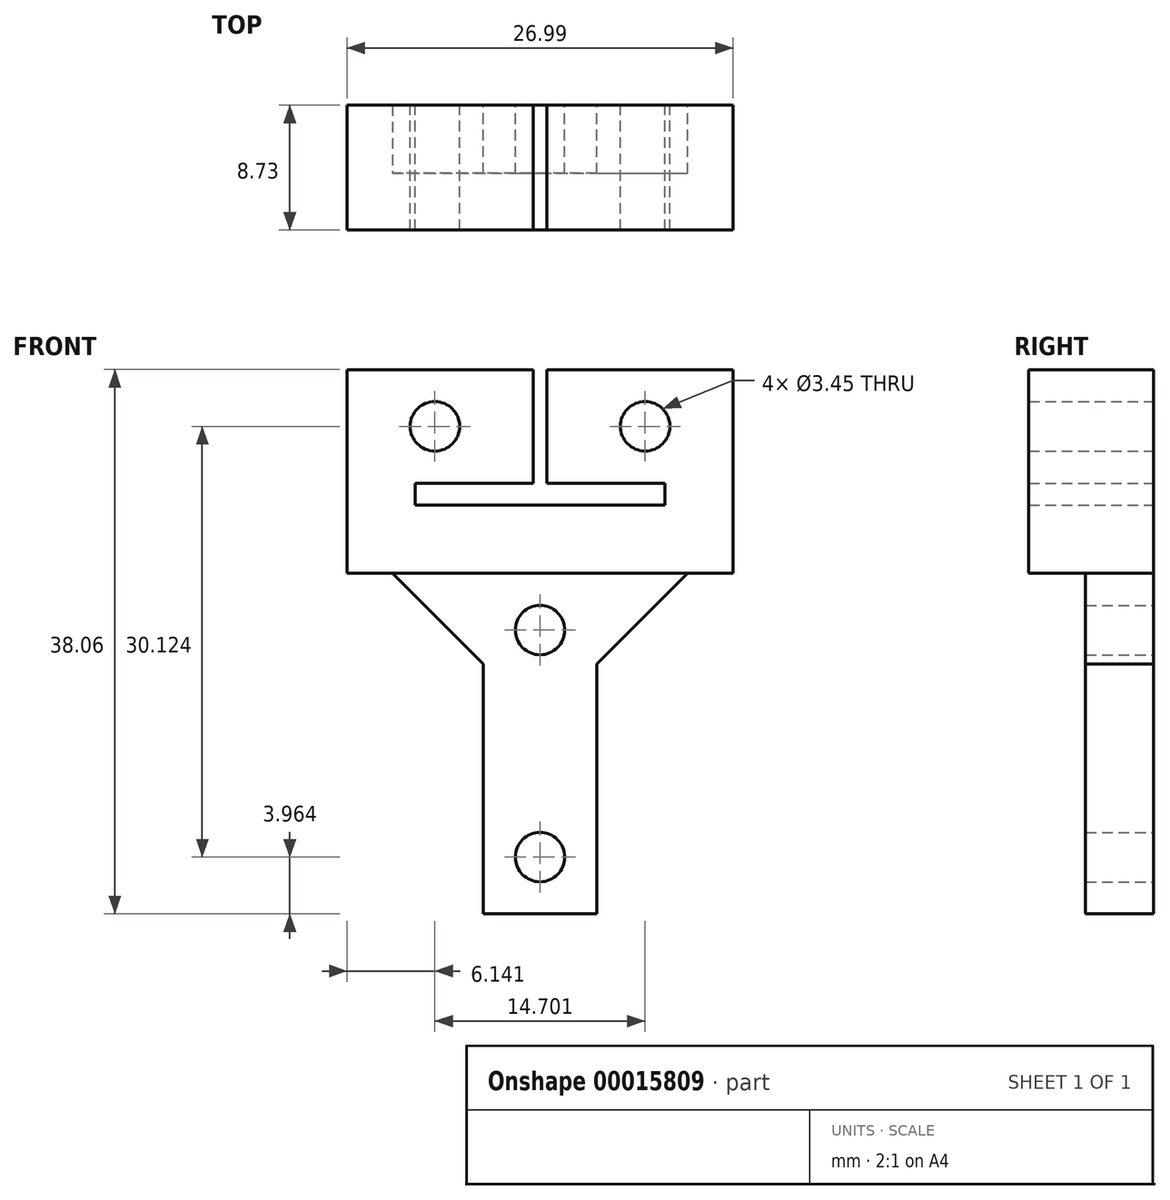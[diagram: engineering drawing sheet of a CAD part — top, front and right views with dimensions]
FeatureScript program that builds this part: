
annotation { "Feature Type Name" : "Feature", "Feature Type Description" : "" }
export const myFeature = defineFeature(function(context is Context, id is Id, definition is map)
    precondition{}
    {
        {
            var Q0;
            Q0=qCreatedBy(makeId("Front.planeOp"),FACE);
            var sketch = newSketch(context, id + "F0", { "sketchPlane" : qUnion([Q0])});
            skLineSegment(sketch, "E0", {"start": v(0, 0) * mm, "end": v(17.46, 0) * mm});
            skLineSegment(sketch, "E1.top", {"start": v(8.26, 9.49) * mm, "end": v(-4.76, 9.49) * mm});
            skLineSegment(sketch, "E1.right", {"start": v(-4.76, -4.76) * mm, "end": v(-4.76, 9.49) * mm});
            skLineSegment(sketch, "E2.top", {"start": v(9.2, 9.49) * mm, "end": v(22.23, 9.49) * mm});
            skLineSegment(sketch, "E2.right", {"start": v(22.23, -4.76) * mm, "end": v(22.23, 9.49) * mm});
            skLineSegment(sketch, "E3", {"start": v(-4.76, -4.76) * mm, "end": v(4.76, -4.76) * mm});
            skLineSegment(sketch, "E4", {"start": v(22.23, -4.76) * mm, "end": v(12.7, -4.76) * mm});
            skLineSegment(sketch, "E5.bottom", {"start": v(12.7, -4.76) * mm, "end": v(4.76, -4.76) * mm, "construction": true});
            skLineSegment(sketch, "E5.top", {"start": v(12.7, -28.58) * mm, "end": v(4.76, -28.58) * mm});
            skLineSegment(sketch, "E5.left", {"start": v(12.7, -4.76) * mm, "end": v(12.7, -28.58) * mm});
            skLineSegment(sketch, "E5.right", {"start": v(4.76, -4.76) * mm, "end": v(4.76, -28.58) * mm});
            skLineSegment(sketch, "E6", {"start": v(0, 0) * mm, "end": v(0, 1.55) * mm});
            skLineSegment(sketch, "E7", {"start": v(17.46, 0) * mm, "end": v(17.46, 1.55) * mm});
            skLineSegment(sketch, "E8.bottom", {"start": v(0, 1.55) * mm, "end": v(8.26, 1.55) * mm});
            skLineSegment(sketch, "E8.right", {"start": v(8.26, 1.55) * mm, "end": v(8.26, 9.49) * mm});
            skLineSegment(sketch, "E9.bottom", {"start": v(17.46, 1.55) * mm, "end": v(9.2, 1.55) * mm});
            skLineSegment(sketch, "E9.right", {"start": v(9.2, 1.55) * mm, "end": v(9.2, 9.49) * mm});
            skLineSegment(sketch, "E10", {"start": v(9.2, 9.49) * mm, "end": v(8.26, 9.49) * mm, "construction": true});
            skLineSegment(sketch, "E11", {"start": v(17.46, 0) * mm, "end": v(17.46, -4.76) * mm});
            skLineSegment(sketch, "E12", {"start": v(17.46, 0) * mm, "end": v(22.23, 0) * mm});
            skLineSegment(sketch, "E13", {"start": v(8.73, -4.76) * mm, "end": v(8.73, -8.73) * mm});
            skLineSegment(sketch, "E14", {"start": v(8.73, -28.58) * mm, "end": v(8.73, -24.6) * mm});
            skCircle(sketch, "E15", {"center": v(8.73, -8.73) * mm, "radius": 1.73 * mm});
            skCircle(sketch, "E16", {"center": v(8.73, -24.6) * mm, "radius": 1.73 * mm});
            skLineSegment(sketch, "E17", {"start": v(9.2, 5.52) * mm, "end": v(16.08, 5.52) * mm});
            skLineSegment(sketch, "E18", {"start": v(8.26, 5.52) * mm, "end": v(1.38, 5.52) * mm});
            skCircle(sketch, "E19", {"center": v(16.08, 5.52) * mm, "radius": 1.73 * mm});
            skCircle(sketch, "E20", {"center": v(1.38, 5.52) * mm, "radius": 1.73 * mm});
            skSolve(sketch);
        }
        {
            var Q0;
            Q0 = qSketchRegion(id + "F0", true);
            extrude(context, id + "F1", {"entities" : qUnion([Q0]), "depth" : 4.76 * mm});
        }
        {
            var Q0;
            Q0=makeQuery(id+"F1.opExtrude","CAP_FACE",FACE,{"disambiguationData":[OSD([sQuery(id+"F0.wireOp",EDGE,"E0"),sQuery(id+"F0.wireOp",EDGE,"E1.top"),sQuery(id+"F0.wireOp",EDGE,"E1.right"),sQuery(id+"F0.wireOp",EDGE,"E2.top"),sQuery(id+"F0.wireOp",EDGE,"E2.right"),sQuery(id+"F0.wireOp",EDGE,"E3"),sQuery(id+"F0.wireOp",EDGE,"E4"),sQuery(id+"F0.wireOp",EDGE,"E5.top"),sQuery(id+"F0.wireOp",EDGE,"E5.left"),sQuery(id+"F0.wireOp",EDGE,"E5.right"),sQuery(id+"F0.wireOp",EDGE,"E6"),sQuery(id+"F0.wireOp",EDGE,"E7"),sQuery(id+"F0.wireOp",EDGE,"E8.bottom"),sQuery(id+"F0.wireOp",EDGE,"E8.right"),sQuery(id+"F0.wireOp",EDGE,"E9.bottom"),sQuery(id+"F0.wireOp",EDGE,"E9.right"),sQuery(id+"F0.wireOp",EDGE,"E15"),sQuery(id+"F0.wireOp",EDGE,"E16"),sQuery(id+"F0.wireOp",EDGE,"E19"),sQuery(id+"F0.wireOp",EDGE,"E20")])],"isStart":false});
            var sketch = newSketch(context, id + "F2", { "sketchPlane" : qUnion([Q0])});
            skLineSegment(sketch, "E21.top", {"start": v(-4.76, -4.76) * mm, "end": v(22.23, -4.76) * mm});
            skLineSegment(sketch, "E21.left", {"start": v(-4.76, 9.49) * mm, "end": v(-4.76, -4.76) * mm});
            skLineSegment(sketch, "E21.right", {"start": v(22.23, 9.49) * mm, "end": v(22.23, -4.76) * mm});
            skLineSegment(sketch, "E22", {"start": v(-4.76, 9.49) * mm, "end": v(8.26, 9.49) * mm});
            skLineSegment(sketch, "E23", {"start": v(8.26, 9.49) * mm, "end": v(8.26, 1.55) * mm});
            skLineSegment(sketch, "E24", {"start": v(8.26, 1.55) * mm, "end": v(0, 1.55) * mm});
            skLineSegment(sketch, "E25", {"start": v(0, 1.55) * mm, "end": v(0, 0) * mm});
            skLineSegment(sketch, "E26", {"start": v(0, 0) * mm, "end": v(17.46, 0) * mm});
            skLineSegment(sketch, "E27", {"start": v(17.46, 0) * mm, "end": v(17.46, 1.55) * mm});
            skLineSegment(sketch, "E28", {"start": v(17.46, 1.55) * mm, "end": v(9.2, 1.55) * mm});
            skLineSegment(sketch, "E29", {"start": v(9.2, 1.55) * mm, "end": v(9.2, 9.49) * mm});
            skLineSegment(sketch, "E30", {"start": v(9.2, 9.49) * mm, "end": v(22.23, 9.49) * mm});
            skCircle(sketch, "E31", {"center": v(1.38, 5.52) * mm, "radius": 1.73 * mm});
            skCircle(sketch, "E32", {"center": v(16.08, 5.52) * mm, "radius": 1.73 * mm});
            skSolve(sketch);
        }
        {
            var Q0;
            Q0 = qSketchRegion(id + "F2", true);
            extrude(context, id + "F3", {"entities" : qUnion([Q0]), "operationType" : NewBodyOperationType.ADD, "depth" : 3.97 * mm});
        }
        {
            var Q0;
            Q0=makeQuery(id+"F1.opExtrude","SWEPT_EDGE",EDGE,{"disambiguationData":[OSD([sQuery(id+"F0.wireOp",EDGE,"E3"),sQuery(id+"F0.wireOp",EDGE,"E5.right")])]});
            var Q1;
            Q1=makeQuery(id+"F1.opExtrude","SWEPT_EDGE",EDGE,{"disambiguationData":[OSD([sQuery(id+"F0.wireOp",EDGE,"E4"),sQuery(id+"F0.wireOp",EDGE,"E5.left")])]});
            chamfer(context, id + "F4", {"entities" : qUnion([Q0, Q1]), "width" : 6.35 * mm, "tangentPropagation" : true});
        }
    });
